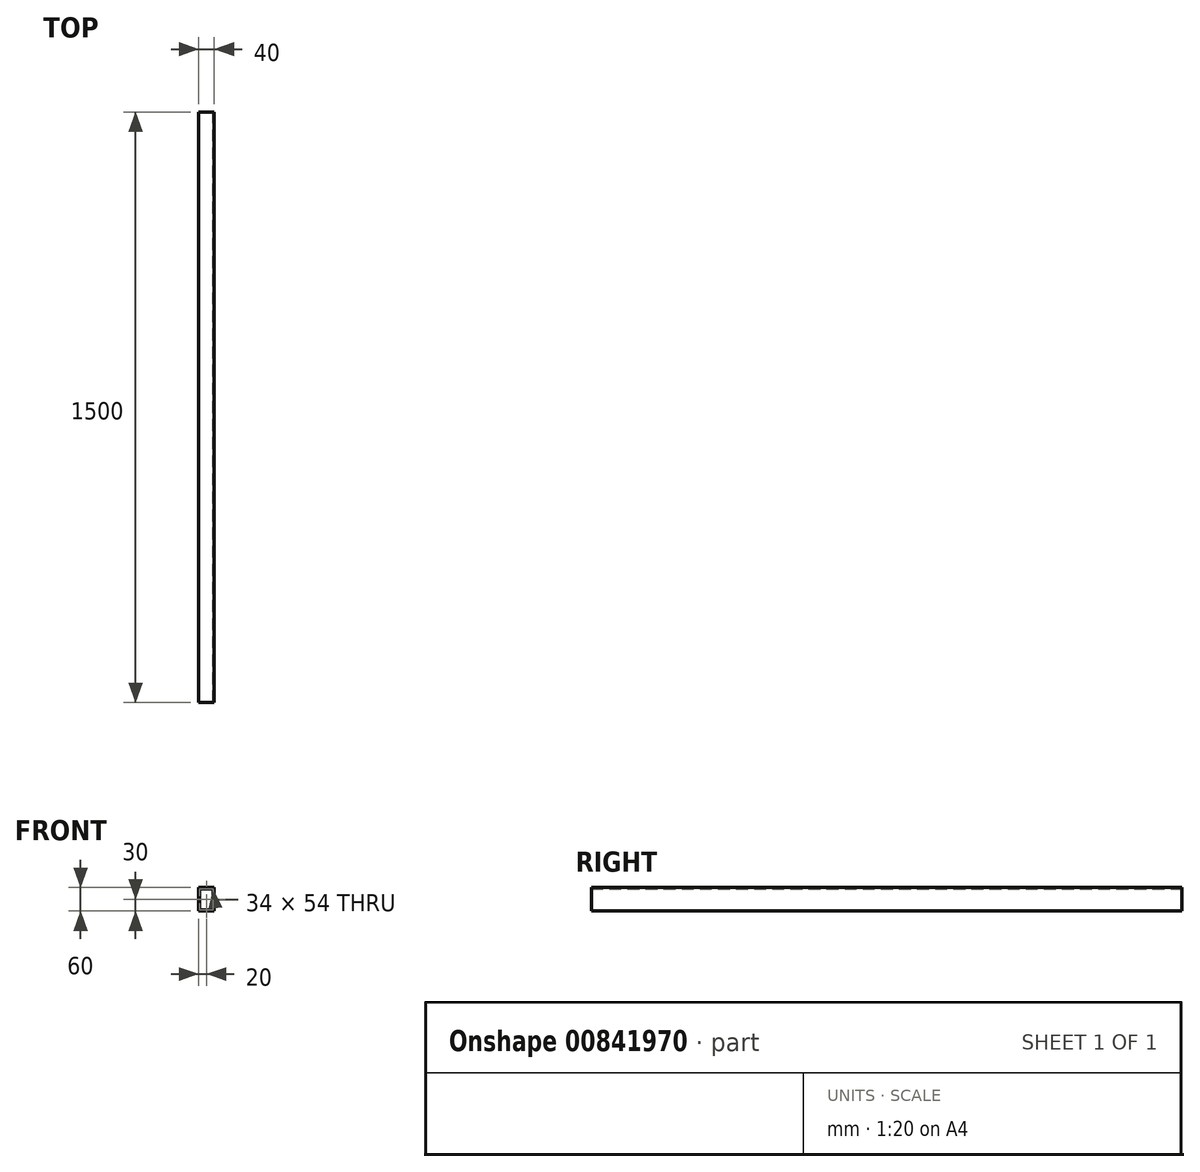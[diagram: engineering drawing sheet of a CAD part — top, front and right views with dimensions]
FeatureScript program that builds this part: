
annotation { "Feature Type Name" : "Feature", "Feature Type Description" : "" }
export const myFeature = defineFeature(function(context is Context, id is Id, definition is map)
    precondition{}
    {
        {
            var Q0;
            Q0=qCreatedBy(makeId("Front.planeOp"),FACE);
            var sketch = newSketch(context, id + "F0", { "sketchPlane" : qUnion([Q0])});
            skLineSegment(sketch, "E0.bottom", {"start": v(-20, 30) * mm, "end": v(20, 30) * mm});
            skLineSegment(sketch, "E0.top", {"start": v(-20, -30) * mm, "end": v(20, -30) * mm});
            skLineSegment(sketch, "E0.left", {"start": v(-20, 30) * mm, "end": v(-20, -30) * mm});
            skLineSegment(sketch, "E0.right", {"start": v(20, 30) * mm, "end": v(20, -30) * mm});
            skLineSegment(sketch, "E1.0", {"start": v(-17, 27) * mm, "end": v(-17, -27) * mm});
            skLineSegment(sketch, "E1.1", {"start": v(-17, 27) * mm, "end": v(17, 27) * mm});
            skLineSegment(sketch, "E1.2", {"start": v(17, 27) * mm, "end": v(17, -27) * mm});
            skLineSegment(sketch, "E1.3", {"start": v(-17, -27) * mm, "end": v(17, -27) * mm});
            skSolve(sketch);
        }
        {
            var Q0;
            Q0=makeQuery(id+"F0.imprint","IMPRINT",FACE,{"disambiguationData":[TD([[makeQuery(id+"F0.imprint","IMPRINT",EDGE,{"derivedFrom":sQuery(id+"F0.wireOp",EDGE,"E0.bottom")}),-1.0]])]});
            extrude(context, id + "F1", {"entities" : qUnion([Q0]), "endBound" : BoundingType.SYMMETRIC, "depth" : 1500 * mm, "offsetDistance" : 25 * mm});
        }
    });
